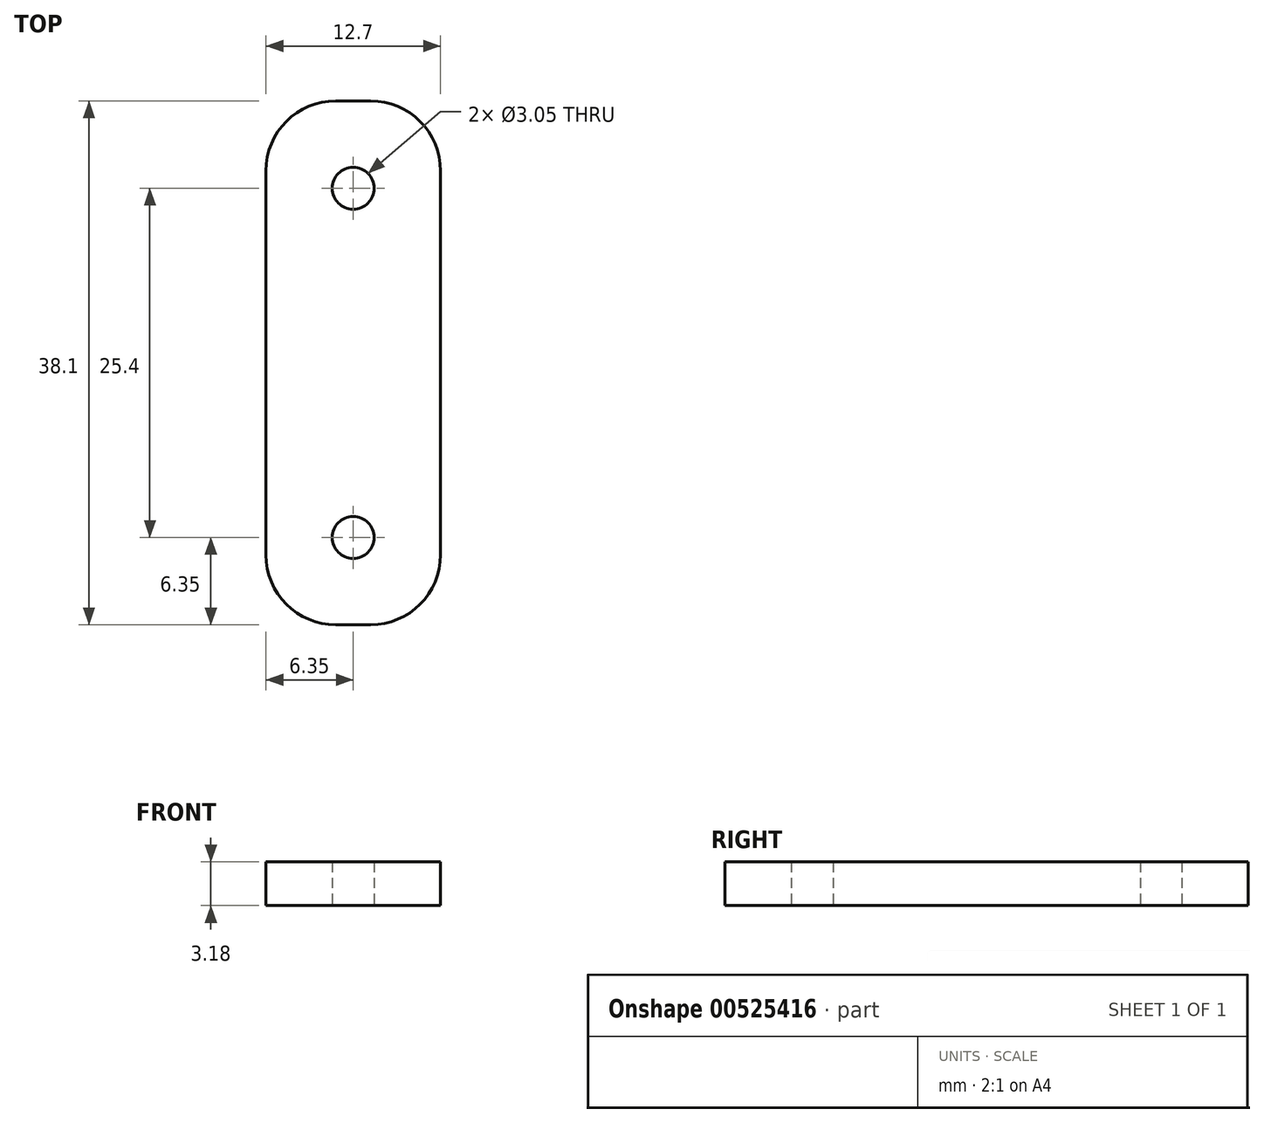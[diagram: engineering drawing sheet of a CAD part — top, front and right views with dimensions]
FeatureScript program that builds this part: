
annotation { "Feature Type Name" : "Feature", "Feature Type Description" : "" }
export const myFeature = defineFeature(function(context is Context, id is Id, definition is map)
    precondition{}
    {
        {
            var Q0;
            Q0=qCreatedBy(makeId("Top.planeOp"),FACE);
            var sketch = newSketch(context, id + "F0", { "sketchPlane" : qUnion([Q0])});
            skLineSegment(sketch, "E0.bottom", {"start": v(1.27, 19.05) * mm, "end": v(-1.27, 19.05) * mm});
            skLineSegment(sketch, "E0.top", {"start": v(1.27, -19.05) * mm, "end": v(-1.27, -19.05) * mm});
            skLineSegment(sketch, "E0.left", {"start": v(6.35, 13.97) * mm, "end": v(6.35, -13.97) * mm});
            skLineSegment(sketch, "E0.right", {"start": v(-6.35, 13.97) * mm, "end": v(-6.35, -13.97) * mm});
            skPoint(sketch, "E0.middle", {"position": v(0, 0) * mm});
            skCircle(sketch, "E1", {"center": v(0, -12.7) * mm, "radius": 1.52 * mm});
            skPoint(sketch, "E2.visualSharp", {"position": v(-6.35, -19.05) * mm});
            skArc(sketch, "E2.filletArc", {"start": v(-6.35, -13.97) * mm, "mid": v(-4.86, -17.56) * mm, "end": v(-1.27, -19.05) * mm});
            skPoint(sketch, "E3.visualSharp", {"position": v(6.35, -19.05) * mm});
            skArc(sketch, "E3.filletArc", {"start": v(1.27, -19.05) * mm, "mid": v(4.86, -17.56) * mm, "end": v(6.35, -13.97) * mm});
            skPoint(sketch, "E4.visualSharp", {"position": v(6.35, 19.05) * mm});
            skArc(sketch, "E4.filletArc", {"start": v(6.35, 13.97) * mm, "mid": v(4.86, 17.56) * mm, "end": v(1.27, 19.05) * mm});
            skPoint(sketch, "E5.visualSharp", {"position": v(-6.35, 19.05) * mm});
            skArc(sketch, "E5.filletArc", {"start": v(-1.27, 19.05) * mm, "mid": v(-4.86, 17.56) * mm, "end": v(-6.35, 13.97) * mm});
            skCircle(sketch, "E6.MirrorC", {"center": v(0, 12.7) * mm, "radius": 1.52 * mm});
            skSolve(sketch);
        }
        {
            var Q0;
            Q0=makeQuery(id+"F0.imprint","IMPRINT",FACE,{"disambiguationData":[TD([[makeQuery(id+"F0.imprint","IMPRINT",EDGE,{"derivedFrom":sQuery(id+"F0.wireOp",EDGE,"E0.bottom")}),1.0]])]});
            extrude(context, id + "F1", {"entities" : qUnion([Q0]), "depth" : 3.17 * mm, "offsetDistance" : 25.4 * mm});
        }
    });
